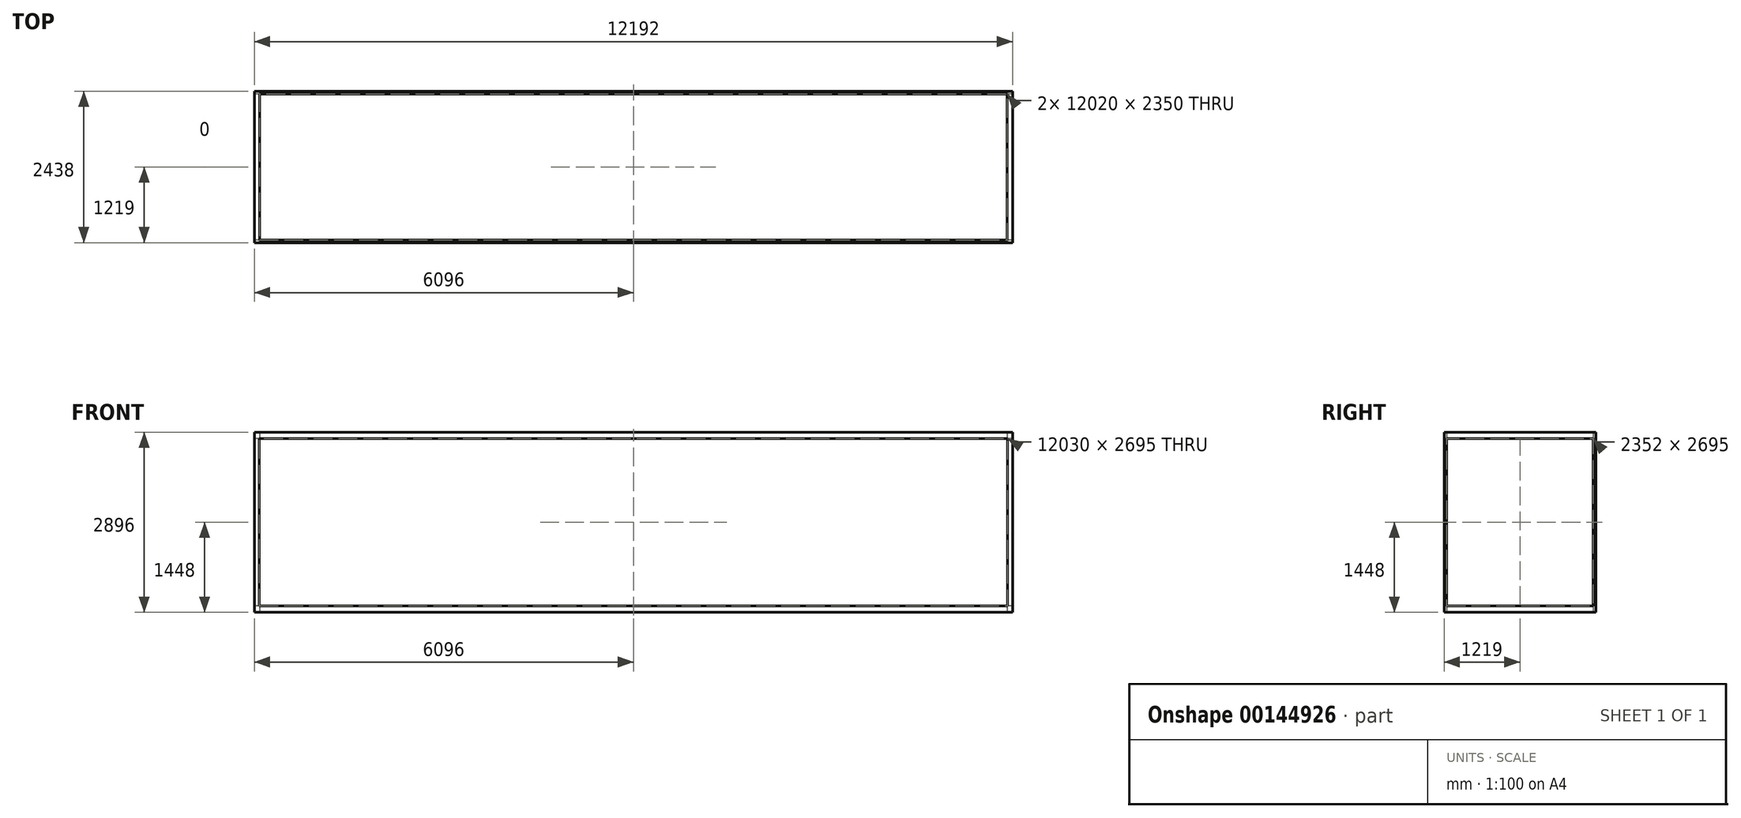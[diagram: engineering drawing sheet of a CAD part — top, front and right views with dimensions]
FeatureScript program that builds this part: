
annotation { "Feature Type Name" : "Feature", "Feature Type Description" : "" }
export const myFeature = defineFeature(function(context is Context, id is Id, definition is map)
    precondition{}
    {
        {
            var Q0;
            Q0=qCreatedBy(makeId("Top.planeOp"),FACE);
            var sketch = newSketch(context, id + "F4", { "sketchPlane" : qUnion([Q0])});
            skLineSegment(sketch, "E0.bottom", {"start": v(6010, -1175) * mm, "end": v(-6010, -1175) * mm});
            skLineSegment(sketch, "E0.top", {"start": v(6010, 1175) * mm, "end": v(-6010, 1175) * mm});
            skLineSegment(sketch, "E0.left", {"start": v(6010, -1175) * mm, "end": v(6010, 1175) * mm});
            skLineSegment(sketch, "E0.right", {"start": v(-6010, -1175) * mm, "end": v(-6010, 1175) * mm});
            skPoint(sketch, "E0.middle", {"position": v(0, 0) * mm});
            skLineSegment(sketch, "E1.bottom", {"start": v(6096, -1219) * mm, "end": v(-6096, -1219) * mm});
            skLineSegment(sketch, "E1.top", {"start": v(6096, 1219) * mm, "end": v(-6096, 1219) * mm});
            skLineSegment(sketch, "E1.left", {"start": v(6096, -1219) * mm, "end": v(6096, 1219) * mm});
            skLineSegment(sketch, "E1.right", {"start": v(-6096, -1219) * mm, "end": v(-6096, 1219) * mm});
            skSolve(sketch);
        }
        {
            var Q0;
            Q0 = qSketchRegion(id + "F4", true);
            extrude(context, id + "F0", {"entities" : qUnion([Q0]), "depth" : 2896 * mm});
        }
        {
            var Q0;
            Q0=makeQuery(id+"F0.opExtrude","SWEPT_FACE",FACE,{"disambiguationData":[OSD([sQuery(id+"F4.wireOp",EDGE,"E1.bottom")])]});
            var sketch = newSketch(context, id + "F1", { "sketchPlane" : qUnion([Q0])});
            skLineSegment(sketch, "E2.bottom", {"start": v(6015, 100.5) * mm, "end": v(-6015, 100.5) * mm});
            skLineSegment(sketch, "E2.top", {"start": v(6015, 2795.5) * mm, "end": v(-6015, 2795.5) * mm});
            skLineSegment(sketch, "E2.left", {"start": v(6015, 100.5) * mm, "end": v(6015, 2795.5) * mm});
            skLineSegment(sketch, "E2.right", {"start": v(-6015, 100.5) * mm, "end": v(-6015, 2795.5) * mm});
            skPoint(sketch, "E2.middle", {"position": v(0, 1448) * mm});
            skSolve(sketch);
        }
        {
            var Q0;
            Q0=makeQuery(id+"F1.imprint","IMPRINT",FACE,{"disambiguationData":[TD([[makeQuery(id+"F1.imprint","IMPRINT",EDGE,{"derivedFrom":sQuery(id+"F1.wireOp",EDGE,"E2.bottom")}),-1.0]])]});
            extrude(context, id + "F5", {"entities" : qUnion([Q0]), "operationType" : NewBodyOperationType.REMOVE, "endBound" : BoundingType.THROUGH_ALL, "oppositeDirection" : true, "depth" : 25 * mm});
        }
        {
            var Q0;
            Q0=makeQuery(id+"F0.opExtrude","SWEPT_FACE",FACE,{"disambiguationData":[OSD([sQuery(id+"F4.wireOp",EDGE,"E1.right")])]});
            var sketch = newSketch(context, id + "F2", { "sketchPlane" : qUnion([Q0])});
            skLineSegment(sketch, "E3.bottom", {"start": v(1176, 100.5) * mm, "end": v(-1176, 100.5) * mm});
            skLineSegment(sketch, "E3.top", {"start": v(1176, 2795.5) * mm, "end": v(-1176, 2795.5) * mm});
            skLineSegment(sketch, "E3.left", {"start": v(1176, 100.5) * mm, "end": v(1176, 2795.5) * mm});
            skLineSegment(sketch, "E3.right", {"start": v(-1176, 100.5) * mm, "end": v(-1176, 2795.5) * mm});
            skPoint(sketch, "E3.middle", {"position": v(0, 1448) * mm});
            skSolve(sketch);
        }
        {
            var Q0;
            Q0=makeQuery(id+"F2.imprint","IMPRINT",FACE,{"disambiguationData":[TD([[makeQuery(id+"F2.imprint","IMPRINT",EDGE,{"derivedFrom":sQuery(id+"F2.wireOp",EDGE,"E3.bottom")}),-1.0]])]});
            extrude(context, id + "F3", {"entities" : qUnion([Q0]), "operationType" : NewBodyOperationType.REMOVE, "endBound" : BoundingType.THROUGH_ALL, "oppositeDirection" : true, "depth" : 25 * mm});
        }
    });
